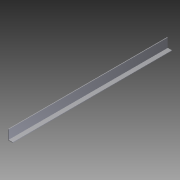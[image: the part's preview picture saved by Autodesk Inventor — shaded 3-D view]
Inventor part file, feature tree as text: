
AUTODESK INVENTOR PART (.ipt)
format: ipt  version: 2012 (Build 160160000, 160)  size: 73,216 bytes
history: native  units: in
note: dims shown in document units (in); Inventor stores cm internally (conversion verified against a paired STEP export)
features: extrude x1, sketch x1
ambient origin geometry x8: Origin, YZ Plane, XZ Plane, XY Plane, X Axis, Y Axis, Z Axis, Center Point
bodies: Solid1 (feature_tree)
feature tree (2):
  extrude  "Extrusion1"  Depth=1.0in
  sketch  "Sketch1"  dims[d0=2.0in d1=1.0in d2=0.125in d3=0.125in d4=33.0in d5=0.0in]
